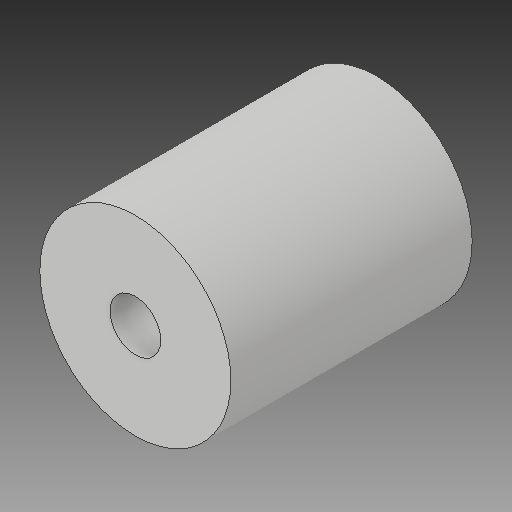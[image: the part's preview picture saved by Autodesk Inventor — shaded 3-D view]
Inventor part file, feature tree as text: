
AUTODESK INVENTOR PART (.ipt)
format: ipt  version: 2019 (Build 230136000, 136)  size: 99,840 bytes
history: native  units: mm
features: extrude x1, sketch x1
ambient origin geometry x8: Origin, YZ Plane, XZ Plane, XY Plane, X Axis, Y Axis, Z Axis, Center Point
bodies: Solid1 (feature_tree)
feature tree (2):
  extrude  "Extrusion1"  Depth=14.5mm
  sketch  "Sketch1"  dims[d0=5.05mm d1=19.0mm d2=9.5mm d3=14.5mm d4=0.0mm d5=0.0mm]
